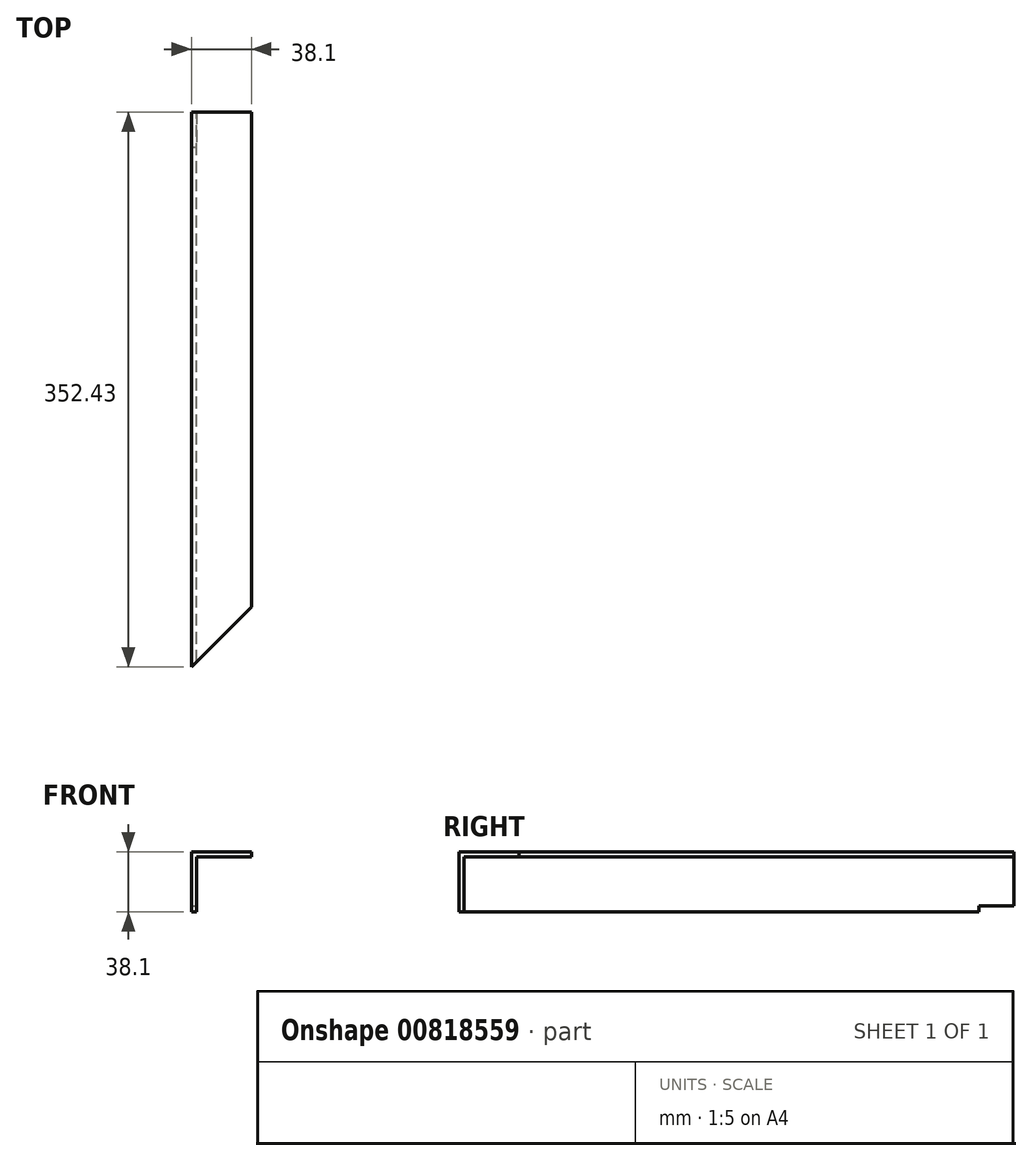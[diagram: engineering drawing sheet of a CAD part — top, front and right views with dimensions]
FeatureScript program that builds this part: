
annotation { "Feature Type Name" : "Feature", "Feature Type Description" : "" }
export const myFeature = defineFeature(function(context is Context, id is Id, definition is map)
    precondition{}
    {
        {
            var Q0;
            Q0=qCreatedBy(makeId("Front.planeOp"),FACE);
            var sketch = newSketch(context, id + "F0", { "sketchPlane" : qUnion([Q0])});
            skLineSegment(sketch, "E0", {"start": v(-21.73, 20.45) * mm, "end": v(-21.73, -17.65) * mm});
            skLineSegment(sketch, "E1", {"start": v(-21.73, -17.65) * mm, "end": v(16.37, -17.65) * mm});
            skLineSegment(sketch, "E2", {"start": v(16.37, -17.65) * mm, "end": v(16.37, -14.47) * mm});
            skLineSegment(sketch, "E3", {"start": v(16.37, -14.47) * mm, "end": v(-18.55, -14.47) * mm});
            skLineSegment(sketch, "E4", {"start": v(-18.55, -14.47) * mm, "end": v(-18.55, 20.45) * mm});
            skLineSegment(sketch, "E5", {"start": v(-18.55, 20.45) * mm, "end": v(-21.73, 20.45) * mm});
            skSolve(sketch);
        }
        {
            var Q0;
            Q0=makeQuery(id+"F0.imprint","IMPRINT",FACE,{"disambiguationData":[TD([[makeQuery(id+"F0.imprint","IMPRINT",EDGE,{"derivedFrom":sQuery(id+"F0.wireOp",EDGE,"E0")}),1.0]])]});
            extrude(context, id + "F1", {"entities" : qUnion([Q0]), "depth" : 352.42 * mm, "offsetDistance" : 25.4 * mm});
        }
        {
            var Q0;
            Q0=makeQuery(id+"F1.opExtrude","SWEPT_FACE",FACE,{"disambiguationData":[OSD([sQuery(id+"F0.wireOp",EDGE,"E4")])]});
            var sketch = newSketch(context, id + "F2", { "sketchPlane" : qUnion([Q0])});
            skLineSegment(sketch, "E6", {"start": v(0, 16.48) * mm, "end": v(-22.23, 16.48) * mm});
            skLineSegment(sketch, "E7", {"start": v(-22.23, 16.48) * mm, "end": v(-22.23, 20.45) * mm});
            skLineSegment(sketch, "E8", {"start": v(-22.23, 20.45) * mm, "end": v(0, 20.45) * mm});
            skLineSegment(sketch, "E9", {"start": v(0, 20.45) * mm, "end": v(0, 16.48) * mm});
            skSolve(sketch);
        }
        {
            var Q0;
            Q0=qSketchRegion(id+"F2",true);
            extrude(context, id + "F3", {"entities" : qUnion([Q0]), "operationType" : NewBodyOperationType.REMOVE, "oppositeDirection" : true, "depth" : 25.4 * mm, "offsetDistance" : 25.4 * mm});
        }
        {
            var Q0;
            Q0=makeQuery(id+"F1.opExtrude","SWEPT_FACE",FACE,{"disambiguationData":[OSD([sQuery(id+"F0.wireOp",EDGE,"E1")])]});
            var sketch = newSketch(context, id + "F4", { "sketchPlane" : qUnion([Q0])});
            skLineSegment(sketch, "E10", {"start": v(-21.73, 352.43) * mm, "end": v(16.37, 352.43) * mm});
            skLineSegment(sketch, "E11", {"start": v(16.37, 352.43) * mm, "end": v(16.37, 314.33) * mm});
            skLineSegment(sketch, "E12", {"start": v(16.37, 314.33) * mm, "end": v(-21.73, 352.43) * mm});
            skSolve(sketch);
        }
        {
            var Q0;
            Q0=qSketchRegion(id+"F4",true);
            extrude(context, id + "F5", {"entities" : qUnion([Q0]), "operationType" : NewBodyOperationType.REMOVE, "oppositeDirection" : true, "depth" : 38.1 * mm, "offsetDistance" : 25.4 * mm});
        }
        {
            var Q0;
            Q0=makeQuery(id+"F1.opExtrude","SWEPT_BODY",BODY,{"disambiguationData":[OSD([sQuery(id+"F0.wireOp",EDGE,"E0"),sQuery(id+"F0.wireOp",EDGE,"E1"),sQuery(id+"F0.wireOp",EDGE,"E2"),sQuery(id+"F0.wireOp",EDGE,"E3"),sQuery(id+"F0.wireOp",EDGE,"E4"),sQuery(id+"F0.wireOp",EDGE,"E5")])]});
            var Q1;
            Q1=makeQuery(id+"F1.opExtrude","SWEPT_FACE",FACE,{"disambiguationData":[OSD([sQuery(id+"F0.wireOp",EDGE,"E1")])]});
            mirror(context, id + "F6", {"operationType" : NewBodyOperationType.ADD, "entities" : qUnion([Q0]), "mirrorPlane" : qUnion([Q1])});
        }
        {
            var Q0;
            {var subQ0=makeQuery(id+"F1.opExtrude","CAP_FACE",FACE,{"disambiguationData":[OSD([sQuery(id+"F0.wireOp",EDGE,"E0"),sQuery(id+"F0.wireOp",EDGE,"E1"),sQuery(id+"F0.wireOp",EDGE,"E2"),sQuery(id+"F0.wireOp",EDGE,"E3"),sQuery(id+"F0.wireOp",EDGE,"E4"),sQuery(id+"F0.wireOp",EDGE,"E5")])],"isStart":true});Q0=makeQuery(id+"F6.boolean.opBoolean","MERGE",FACE,{"derivedFrom":[subQ0,makeQuery(id+"F6.opPattern","COPY",FACE,{"derivedFrom":subQ0,"instanceName":"1"})]});}
            var sketch = newSketch(context, id + "F7", { "sketchPlane" : qUnion([Q0])});
            skLineSegment(sketch, "E13", {"start": v(21.73, -17.65) * mm, "end": v(-16.37, -17.65) * mm});
            skLineSegment(sketch, "E14", {"start": v(-16.37, -17.65) * mm, "end": v(-16.37, 20.45) * mm});
            skLineSegment(sketch, "E15", {"start": v(-16.37, 20.45) * mm, "end": v(21.73, 20.45) * mm});
            skLineSegment(sketch, "E16", {"start": v(21.73, 20.45) * mm, "end": v(21.73, -17.65) * mm});
            skSolve(sketch);
        }
        {
            var Q0;
            Q0 = qSketchRegion(id + "F7", true);
            extrude(context, id + "F8", {"entities" : qUnion([Q0]), "operationType" : NewBodyOperationType.REMOVE, "endBound" : BoundingType.THROUGH_ALL, "oppositeDirection" : true, "depth" : 25.4 * mm, "offsetDistance" : 25.4 * mm});
        }
    });
